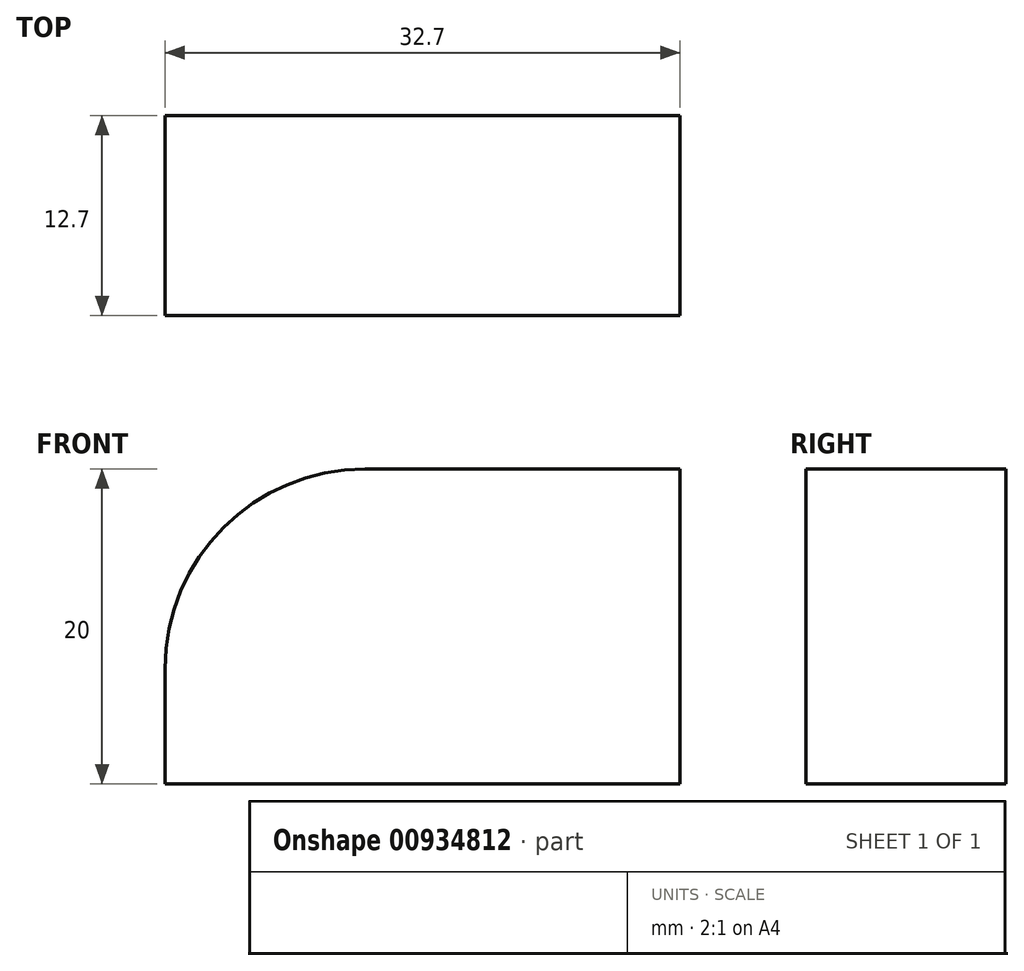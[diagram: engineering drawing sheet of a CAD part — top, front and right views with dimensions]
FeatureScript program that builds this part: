
annotation { "Feature Type Name" : "Feature", "Feature Type Description" : "" }
export const myFeature = defineFeature(function(context is Context, id is Id, definition is map)
    precondition{}
    {
        {
            var Q0;
            Q0=qCreatedBy(makeId("Front.planeOp"),FACE);
            var sketch = newSketch(context, id + "F0", { "sketchPlane" : qUnion([Q0])});
            skLineSegment(sketch, "E0.bottom", {"start": v(-32.7, 1.1) * mm, "end": v(0, 1.1) * mm});
            skLineSegment(sketch, "E0.top", {"start": v(-20, 21.1) * mm, "end": v(0, 21.1) * mm});
            skLineSegment(sketch, "E0.left", {"start": v(-32.7, 1.1) * mm, "end": v(-32.7, 8.4) * mm});
            skLineSegment(sketch, "E0.right", {"start": v(0, 1.1) * mm, "end": v(0, 21.1) * mm});
            skPoint(sketch, "E1.visualSharp", {"position": v(-32.7, 21.1) * mm});
            skArc(sketch, "E1.filletArc", {"start": v(-20, 21.1) * mm, "mid": v(-28.98, 17.38) * mm, "end": v(-32.7, 8.4) * mm});
            skSolve(sketch);
        }
        {
            var Q0;
            Q0=makeQuery(id+"F0.imprint","IMPRINT",FACE,{"disambiguationData":[TD([[makeQuery(id+"F0.imprint","IMPRINT",EDGE,{"derivedFrom":sQuery(id+"F0.wireOp",EDGE,"E0.bottom")}),1.0]])]});
            extrude(context, id + "F1", {"entities" : qUnion([Q0]), "depth" : 12.7 * mm, "offsetDistance" : 25 * mm});
        }
    });
